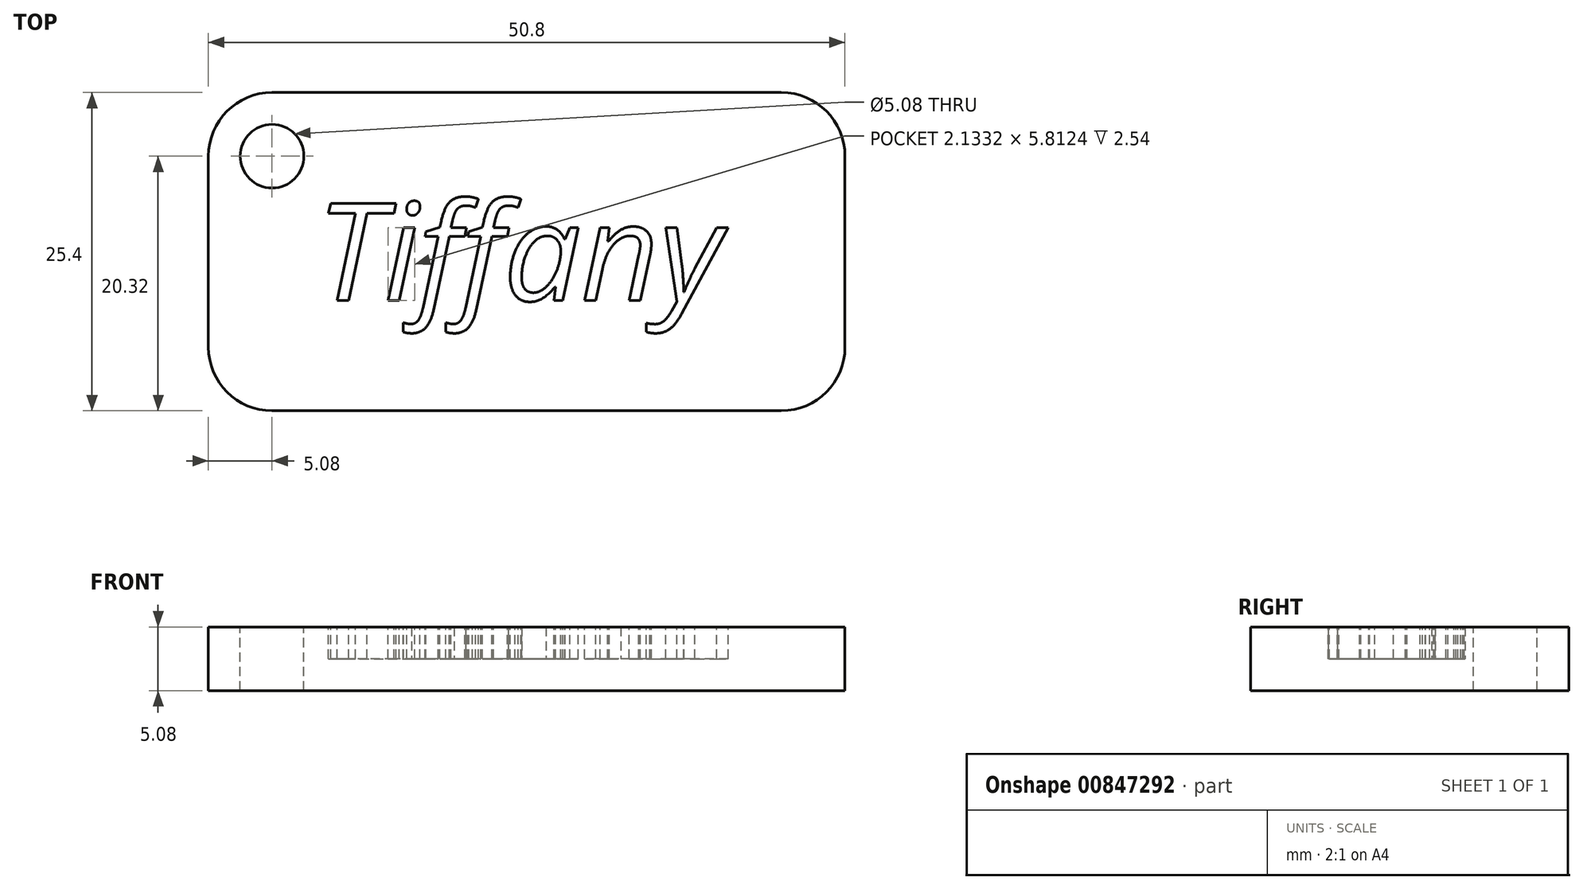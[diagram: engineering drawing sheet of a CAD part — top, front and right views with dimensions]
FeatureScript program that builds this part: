
annotation { "Feature Type Name" : "Feature", "Feature Type Description" : "" }
export const myFeature = defineFeature(function(context is Context, id is Id, definition is map)
    precondition{}
    {
        {
            var Q0;
            Q0=qCreatedBy(makeId("Top.planeOp"),FACE);
            var sketch = newSketch(context, id + "F0", { "sketchPlane" : qUnion([Q0])});
            skLineSegment(sketch, "E0.bottom", {"start": v(25.4, -12.7) * mm, "end": v(-25.4, -12.7) * mm});
            skLineSegment(sketch, "E0.top", {"start": v(25.4, 12.7) * mm, "end": v(-25.4, 12.7) * mm});
            skLineSegment(sketch, "E0.left", {"start": v(25.4, -12.7) * mm, "end": v(25.4, 12.7) * mm});
            skLineSegment(sketch, "E0.right", {"start": v(-25.4, -12.7) * mm, "end": v(-25.4, 12.7) * mm});
            skPoint(sketch, "E0.middle", {"position": v(0, 0) * mm});
            skSolve(sketch);
        }
        {
            var Q0;
            Q0=makeQuery(id+"F0.imprint","IMPRINT",FACE,{"disambiguationData":[TD([[makeQuery(id+"F0.imprint","IMPRINT",EDGE,{"derivedFrom":sQuery(id+"F0.wireOp",EDGE,"E0.bottom")}),-1.0]])]});
            extrude(context, id + "F1", {"entities" : qUnion([Q0]), "depth" : 5.08 * mm, "offsetDistance" : 25.4 * mm});
        }
        {
            var Q0;
            Q0=makeQuery(id+"F1.opExtrude","CAP_FACE",FACE,{"disambiguationData":[OSD([sQuery(id+"F0.wireOp",EDGE,"E0.bottom"),sQuery(id+"F0.wireOp",EDGE,"E0.top"),sQuery(id+"F0.wireOp",EDGE,"E0.left"),sQuery(id+"F0.wireOp",EDGE,"E0.right")])],"isStart":false});
            var sketch = newSketch(context, id + "F2", { "sketchPlane" : qUnion([Q0])});
            skText(sketch, "E1", { "text": "Tiffany", "fontName": "OpenSans-Italic.ttf"});
            skLineSegment(sketch, "E2", {"start": v(-16.8, 0) * mm, "end": v(16.8, 0) * mm, "construction": true});
            skPoint(sketch, "E3", {"position": v(0, 0) * mm});
            const initialGuessF2  = {"E1": [-0.0168, -0.00391, 1, 0, 0.00782]};
            skSetInitialGuess(sketch, initialGuessF2);
            skSolve(sketch);
        }
        {
            var Q0;
            Q0 = qSketchRegion(id + "F2", true);
            extrude(context, id + "F3", {"entities" : qUnion([Q0]), "operationType" : NewBodyOperationType.REMOVE, "oppositeDirection" : true, "depth" : 2.54 * mm, "offsetDistance" : 25.4 * mm});
        }
        {
            var Q0;
            Q0=makeQuery(id+"F1.opExtrude","SWEPT_EDGE",EDGE,{"disambiguationData":[OSD([sQuery(id+"F0.wireOp",EDGE,"E0.bottom"),sQuery(id+"F0.wireOp",EDGE,"E0.left")])]});
            var Q1;
            Q1=makeQuery(id+"F1.opExtrude","SWEPT_EDGE",EDGE,{"disambiguationData":[OSD([sQuery(id+"F0.wireOp",EDGE,"E0.top"),sQuery(id+"F0.wireOp",EDGE,"E0.left")])]});
            var Q2;
            Q2=makeQuery(id+"F1.opExtrude","SWEPT_EDGE",EDGE,{"disambiguationData":[OSD([sQuery(id+"F0.wireOp",EDGE,"E0.top"),sQuery(id+"F0.wireOp",EDGE,"E0.right")])]});
            var Q3;
            Q3=makeQuery(id+"F1.opExtrude","SWEPT_EDGE",EDGE,{"disambiguationData":[OSD([sQuery(id+"F0.wireOp",EDGE,"E0.bottom"),sQuery(id+"F0.wireOp",EDGE,"E0.right")])]});
            fillet(context, id + "F4", {"entities" : qUnion([Q0, Q1, Q2, Q3]), "radius" : 5.08 * mm, "tangentPropagation" : true, "allowEdgeOverflow" : false});
        }
        {
            var Q0;
            {var subQ0=sQuery(id+"F0.wireOp",EDGE,"E0.top");var subQ1=sQuery(id+"F0.wireOp",EDGE,"E0.right");var subQ2=sQuery(id+"F0.wireOp",EDGE,"E0.bottom");var subQ3=sQuery(id+"F0.wireOp",EDGE,"E0.left");Q0=makeQuery(id+"F3.boolean.opBoolean","SPLIT",FACE,{"disambiguationData":[TD([makeQuery(id+"F1.opExtrude","SWEPT_FACE",FACE,{"disambiguationData":[OSD([subQ2])]})])],"derivedFrom":makeQuery(id+"F1.opExtrude","CAP_FACE",FACE,{"disambiguationData":[OSD([subQ2,subQ0,subQ3,subQ1])],"isStart":false})});}
            var sketch = newSketch(context, id + "F5", { "sketchPlane" : qUnion([Q0])});
            skCircle(sketch, "E4", {"center": v(-20.32, 7.62) * mm, "radius": 2.54 * mm});
            skSolve(sketch);
        }
        {
            var Q0;
            Q0=makeQuery(id+"F5.imprint","IMPRINT",FACE,{"disambiguationData":[TD([[makeQuery(id+"F5.imprint","IMPRINT",EDGE,{"derivedFrom":sQuery(id+"F5.wireOp",EDGE,"E4")}),1.0]])]});
            extrude(context, id + "F6", {"entities" : qUnion([Q0]), "operationType" : NewBodyOperationType.REMOVE, "oppositeDirection" : true, "depth" : 25.4 * mm, "offsetDistance" : 25.4 * mm});
        }
    });
